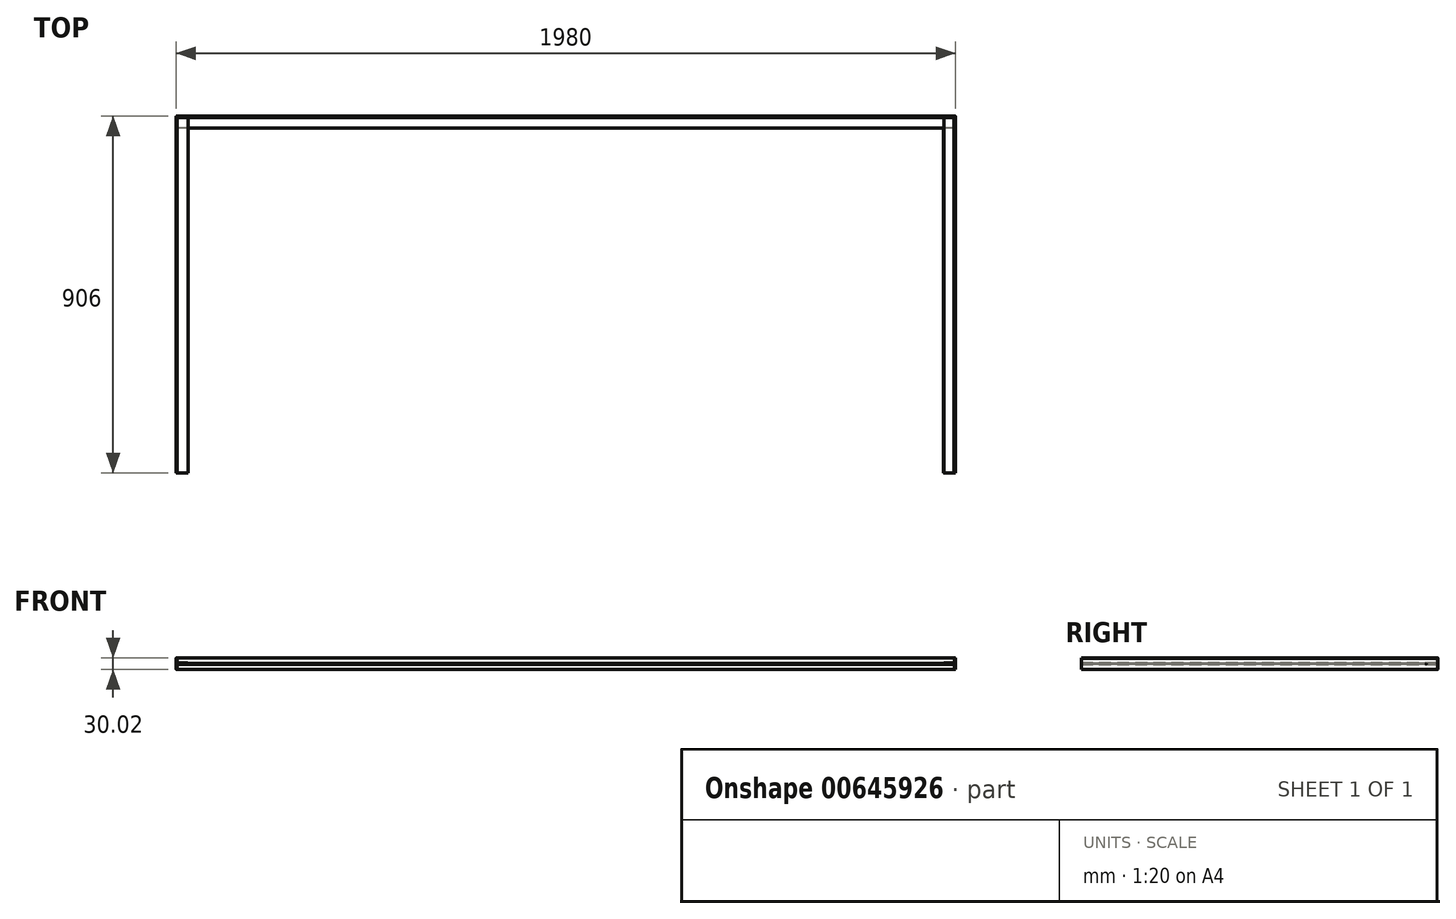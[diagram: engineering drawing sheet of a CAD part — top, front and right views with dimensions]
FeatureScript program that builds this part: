
annotation { "Feature Type Name" : "Feature", "Feature Type Description" : "" }
export const myFeature = defineFeature(function(context is Context, id is Id, definition is map)
    precondition{}
    {
        {
            var Q0;
            Q0=qCreatedBy(makeId("Right.planeOp"),FACE);
            var sketch = newSketch(context, id + "F0", { "sketchPlane" : qUnion([Q0])});
            skLineSegment(sketch, "E0", {"start": v(0, 1) * mm, "end": v(0, 29) * mm});
            skLineSegment(sketch, "E1", {"start": v(-1, 30) * mm, "end": v(-2, 30) * mm});
            skLineSegment(sketch, "E2", {"start": v(-3, 29) * mm, "end": v(-3, 16.94) * mm});
            skLineSegment(sketch, "E3", {"start": v(-2, 0) * mm, "end": v(-1, 0) * mm});
            skLineSegment(sketch, "E4.0", {"start": v(-29, 12.94) * mm, "end": v(-4, 12.94) * mm});
            skLineSegment(sketch, "E5.0", {"start": v(-29, 15.94) * mm, "end": v(-4, 15.94) * mm});
            skLineSegment(sketch, "E6.0", {"start": v(-30, 13.94) * mm, "end": v(-30, 14.94) * mm});
            skLineSegment(sketch, "E7.trimOffspring", {"start": v(-3, 11.94) * mm, "end": v(-3, 1) * mm});
            skPoint(sketch, "E8.visualSharp", {"position": v(-30, 12.94) * mm});
            skArc(sketch, "E8.filletArc", {"start": v(-30, 13.94) * mm, "mid": v(-29.7, 13.23) * mm, "end": v(-29, 12.94) * mm});
            skPoint(sketch, "E9.visualSharp", {"position": v(-30, 15.94) * mm});
            skArc(sketch, "E9.filletArc", {"start": v(-29, 15.94) * mm, "mid": v(-29.7, 15.64) * mm, "end": v(-30, 14.94) * mm});
            skPoint(sketch, "E10.visualSharp", {"position": v(-3, 15.94) * mm});
            skArc(sketch, "E10.filletArc", {"start": v(-4, 15.94) * mm, "mid": v(-3.3, 16.23) * mm, "end": v(-3, 16.94) * mm});
            skPoint(sketch, "E11.visualSharp", {"position": v(-3, 12.94) * mm});
            skArc(sketch, "E11.filletArc", {"start": v(-3, 11.94) * mm, "mid": v(-3.3, 12.64) * mm, "end": v(-4, 12.94) * mm});
            skPoint(sketch, "E12.visualSharp", {"position": v(-3, 0) * mm});
            skArc(sketch, "E12.filletArc", {"start": v(-3, 1) * mm, "mid": v(-2.7, 0.3) * mm, "end": v(-2, 0) * mm});
            skPoint(sketch, "E13.visualSharp", {"position": v(0, 0) * mm});
            skArc(sketch, "E13.filletArc", {"start": v(-1, 0) * mm, "mid": v(-0.3, 0.3) * mm, "end": v(0, 1) * mm});
            skPoint(sketch, "E14.visualSharp", {"position": v(-3, 30) * mm});
            skArc(sketch, "E14.filletArc", {"start": v(-2, 30) * mm, "mid": v(-2.7, 29.7) * mm, "end": v(-3, 29) * mm});
            skPoint(sketch, "E15.visualSharp", {"position": v(0, 30) * mm});
            skArc(sketch, "E15.filletArc", {"start": v(0, 29) * mm, "mid": v(-0.3, 29.7) * mm, "end": v(-1, 30) * mm});
            skSolve(sketch);
        }
        {
            var Q0;
            Q0 = qSketchRegion(id + "F0", true);
            extrude(context, id + "F1", {"entities" : qUnion([Q0]), "depth" : 1980 * mm, "offsetDistance" : 25 * mm});
        }
        {
            var Q0;
            Q0=makeQuery(id+"F1.opExtrude","SWEPT_BODY",BODY,{"disambiguationData":[OSD([sQuery(id+"F0.wireOp",EDGE,"E0"),sQuery(id+"F0.wireOp",EDGE,"E1"),sQuery(id+"F0.wireOp",EDGE,"E2"),sQuery(id+"F0.wireOp",EDGE,"E3"),sQuery(id+"F0.wireOp",EDGE,"E4.0"),sQuery(id+"F0.wireOp",EDGE,"E5.0"),sQuery(id+"F0.wireOp",EDGE,"E6.0"),sQuery(id+"F0.wireOp",EDGE,"E7.trimOffspring"),sQuery(id+"F0.wireOp",EDGE,"E8.filletArc"),sQuery(id+"F0.wireOp",EDGE,"E9.filletArc"),sQuery(id+"F0.wireOp",EDGE,"E10.filletArc"),sQuery(id+"F0.wireOp",EDGE,"E11.filletArc"),sQuery(id+"F0.wireOp",EDGE,"E12.filletArc"),sQuery(id+"F0.wireOp",EDGE,"E13.filletArc"),sQuery(id+"F0.wireOp",EDGE,"E14.filletArc"),sQuery(id+"F0.wireOp",EDGE,"E15.filletArc")])]});
            var Q1;
            Q1=qCreatedBy(makeId("Front.planeOp"),FACE);
            transform(context, id + "F2", {"entities" : qUnion([Q0]), "transformType" : TransformType.TRANSLATION_DISTANCE, "transformDirection" : qUnion([Q1]), "distance" : 906 * mm, "oppositeDirection" : true, "makeCopy" : false});
        }
        {
            var Q0;
            Q0=qCreatedBy(makeId("Front.planeOp"),FACE);
            var sketch = newSketch(context, id + "F3", { "sketchPlane" : qUnion([Q0])});
            skLineSegment(sketch, "E16", {"start": v(0, 1) * mm, "end": v(0, 29) * mm});
            skArc(sketch, "E17.MirrorCS", {"start": v(0, 29) * mm, "mid": v(0.3, 29.7) * mm, "end": v(1, 30) * mm});
            skArc(sketch, "E18.MirrorCS", {"start": v(1, 0) * mm, "mid": v(0.3, 0.3) * mm, "end": v(0, 1) * mm});
            skLineSegment(sketch, "E19.MirrorCS", {"start": v(2, 0) * mm, "end": v(1, 0) * mm});
            skArc(sketch, "E20.MirrorCS", {"start": v(2, 30) * mm, "mid": v(2.7, 29.7) * mm, "end": v(3, 29) * mm});
            skArc(sketch, "E21.MirrorCS", {"start": v(4, 16.5) * mm, "mid": v(3.3, 16.8) * mm, "end": v(3, 17.5) * mm});
            skLineSegment(sketch, "E22.MirrorCS", {"start": v(1, 30) * mm, "end": v(2, 30) * mm});
            skLineSegment(sketch, "E23.MirrorCS", {"start": v(30, 14.5) * mm, "end": v(30, 15.5) * mm});
            skArc(sketch, "E24.MirrorCS", {"start": v(3, 1) * mm, "mid": v(2.7, 0.3) * mm, "end": v(2, 0) * mm});
            skArc(sketch, "E25.MirrorCS", {"start": v(29, 16.5) * mm, "mid": v(29.7, 16.2) * mm, "end": v(30, 15.5) * mm});
            skArc(sketch, "E26.MirrorCS", {"start": v(30, 14.5) * mm, "mid": v(29.7, 13.8) * mm, "end": v(29, 13.5) * mm});
            skArc(sketch, "E27.MirrorCS", {"start": v(3, 12.5) * mm, "mid": v(3.3, 13.2) * mm, "end": v(4, 13.5) * mm});
            skPoint(sketch, "E28.MirrorP", {"position": v(3, 16.5) * mm});
            skLineSegment(sketch, "E29.MirrorCS", {"start": v(3, 29) * mm, "end": v(3, 17.5) * mm});
            skPoint(sketch, "E30.MirrorP", {"position": v(30, 13.5) * mm});
            skPoint(sketch, "E31.MirrorP", {"position": v(3, 0) * mm});
            skPoint(sketch, "E32.MirrorP", {"position": v(3, 30) * mm});
            skLineSegment(sketch, "E33.MirrorCS", {"start": v(29, 16.5) * mm, "end": v(4, 16.5) * mm});
            skLineSegment(sketch, "E34.MirrorCS", {"start": v(29, 13.5) * mm, "end": v(4, 13.5) * mm});
            skLineSegment(sketch, "E35.MirrorCS", {"start": v(3, 12.5) * mm, "end": v(3, 1) * mm});
            skPoint(sketch, "E36.MirrorP", {"position": v(30, 16.5) * mm});
            skPoint(sketch, "E37.MirrorP", {"position": v(3, 13.5) * mm});
            skSolve(sketch);
        }
        {
            var Q0;
            Q0 = qSketchRegion(id + "F3", true);
            extrude(context, id + "F4", {"entities" : qUnion([Q0]), "operationType" : NewBodyOperationType.ADD, "oppositeDirection" : true, "depth" : 906 * mm, "offsetDistance" : 25 * mm});
        }
        {
            var Q0;
            Q0=qCreatedBy(makeId("Front.planeOp"),FACE);
            var sketch = newSketch(context, id + "F5", { "sketchPlane" : qUnion([Q0])});
            skLineSegment(sketch, "E38", {"start": v(1980, 0.93) * mm, "end": v(1980, 28.93) * mm});
            skPoint(sketch, "E39.visualSharp", {"position": v(1980, 29.98) * mm});
            skArc(sketch, "E40.MirrorCS", {"start": v(1950.97, 13.48) * mm, "mid": v(1950.27, 13.79) * mm, "end": v(1950, 14.5) * mm});
            skArc(sketch, "E41.MirrorCS", {"start": v(1950, 15.5) * mm, "mid": v(1950.29, 16.19) * mm, "end": v(1950.97, 16.48) * mm});
            skLineSegment(sketch, "E42.MirrorCS", {"start": v(1977.97, 29.98) * mm, "end": v(1979.05, 29.98) * mm});
            skLineSegment(sketch, "E43.MirrorCS", {"start": v(1950, 14.5) * mm, "end": v(1950, 15.5) * mm});
            skLineSegment(sketch, "E44.MirrorCS", {"start": v(1977.97, -0.02) * mm, "end": v(1979.05, -0.02) * mm});
            skArc(sketch, "E45.MirrorCS", {"start": v(1977, 17.43) * mm, "mid": v(1976.7, 16.77) * mm, "end": v(1976.05, 16.48) * mm});
            skArc(sketch, "E46.MirrorCS", {"start": v(1976.05, 13.48) * mm, "mid": v(1976.74, 13.15) * mm, "end": v(1977, 12.43) * mm});
            skArc(sketch, "E47.MirrorCS", {"start": v(1977.97, -0.02) * mm, "mid": v(1977.27, 0.29) * mm, "end": v(1977, 1) * mm});
            skArc(sketch, "E48.MirrorCS", {"start": v(1977, 29) * mm, "mid": v(1977.29, 29.69) * mm, "end": v(1977.97, 29.98) * mm});
            skArc(sketch, "E49.MirrorCS", {"start": v(1979.05, 29.98) * mm, "mid": v(1979.74, 29.65) * mm, "end": v(1980, 28.93) * mm});
            skArc(sketch, "E50.MirrorCS", {"start": v(1980, 0.93) * mm, "mid": v(1979.7, 0.27) * mm, "end": v(1979.05, -0.02) * mm});
            skPoint(sketch, "E51.MirrorP", {"position": v(1950, 13.48) * mm});
            skPoint(sketch, "E52.MirrorP", {"position": v(1977, -0.02) * mm});
            skPoint(sketch, "E53.MirrorP", {"position": v(1977, 13.48) * mm});
            skPoint(sketch, "E54.MirrorP", {"position": v(1977, 29.98) * mm});
            skPoint(sketch, "E55.MirrorP", {"position": v(1950, 16.48) * mm});
            skPoint(sketch, "E56.MirrorP", {"position": v(1977, 16.48) * mm});
            skLineSegment(sketch, "E57.MirrorCS", {"start": v(1977, 12.43) * mm, "end": v(1977, 1) * mm});
            skLineSegment(sketch, "E58.MirrorCS", {"start": v(1950.97, 13.48) * mm, "end": v(1976.05, 13.48) * mm});
            skLineSegment(sketch, "E59.MirrorCS", {"start": v(1977, 29) * mm, "end": v(1977, 17.43) * mm});
            skLineSegment(sketch, "E60.MirrorCS", {"start": v(1950.97, 16.48) * mm, "end": v(1976.05, 16.48) * mm});
            skSolve(sketch);
        }
        {
            var Q0;
            Q0=makeQuery(id+"F5.imprint","IMPRINT",FACE,{"disambiguationData":[TD([[makeQuery(id+"F5.imprint","IMPRINT",EDGE,{"derivedFrom":sQuery(id+"F5.wireOp",EDGE,"E38")}),1.0]])]});
            extrude(context, id + "F6", {"entities" : qUnion([Q0]), "operationType" : NewBodyOperationType.ADD, "oppositeDirection" : true, "depth" : 906 * mm, "offsetDistance" : 25 * mm});
        }
        {
            var Q0;
            Q0 = qSketchRegion(id + "F3", true);
            extrude(context, id + "F7", {"entities" : qUnion([Q0]), "operationType" : NewBodyOperationType.ADD, "oppositeDirection" : true, "depth" : 906 * mm, "offsetDistance" : 25 * mm});
        }
    });
